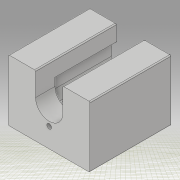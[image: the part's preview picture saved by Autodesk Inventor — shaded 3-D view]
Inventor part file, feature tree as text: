
AUTODESK INVENTOR PART (.ipt)
format: ipt  version: 2018 (Build 220112000, 112)  size: 278,528 bytes
history: native  units: in
note: dims shown in document units (in); Inventor stores cm internally (conversion verified against a paired STEP export)
features: extrude x7, sketch x7, plane x3, fillet x2, projected_geometry x2, mirror x1
ambient origin geometry x8: Origin, YZ Plane, XZ Plane, XY Plane, X Axis, Y Axis, Z Axis, Center Point
bodies: Solid1 (feature_tree)
feature tree (22):
  extrude  "Extrusion1"  Depth=2.0in
  extrude  "Extrusion2"  Depth=0.911in
  extrude  "Extrusion3"  Depth=0.385in
  plane  "Work Plane1"
  extrude  "Extrusion4"  Depth=0.05in
  fillet  "Fillet1"  Radius=0.05in
  extrude  "Extrusion5"  Depth=2.0in TaperAngle=0.0deg
  extrude  "Extrusion6"  Depth=0.05in TaperAngle=0.0deg
  plane  "Work Plane2"
  plane  "Work Plane3"
  mirror  "Mirror3"
  fillet  "Fillet3"  Radius=2.0in
  extrude  "Extrusion7"  Depth=0.025in
  sketch  "Sketch1"  dims[d0=2.0in d1=2.0in]
  sketch  "Sketch2"  dims[d2=1.5in d3=0.0in d4=0.911in]
  projected_geometry  "Projected Loop1"
  sketch  "Sketch3"  dims[d5=0.681in d6=0.385in]
  sketch  "Sketch4"  dims[d7=0.77in d8=0.05in d9=0.05in]
  sketch  "Sketch5"  dims[d10=0.17in d12=2.0in d13=0.0in]
  sketch  "Sketch6"  dims[d14=0.911in d15=0.681in d16=0.385in d17=0.77in d18=0.05in d19=0.05in d20=0.17in d21=0.5in d22=0.0in]
  sketch  "Sketch8"  dims[d23=0.911in d24=0.681in d25=0.385in d26=0.77in d27=0.05in d28=0.05in d29=0.17in d30=2.0in d31=0.0in d32=0.025in d33=0.025in d34=0.0in d35=0.05in d36=0.05in d37=0.05in d38=0.05in d39=1.0in d40=0.0in d43=0.025in d44=0.115in d45=1.0in d46=0.0in]
  projected_geometry  "Projected Loop2"
